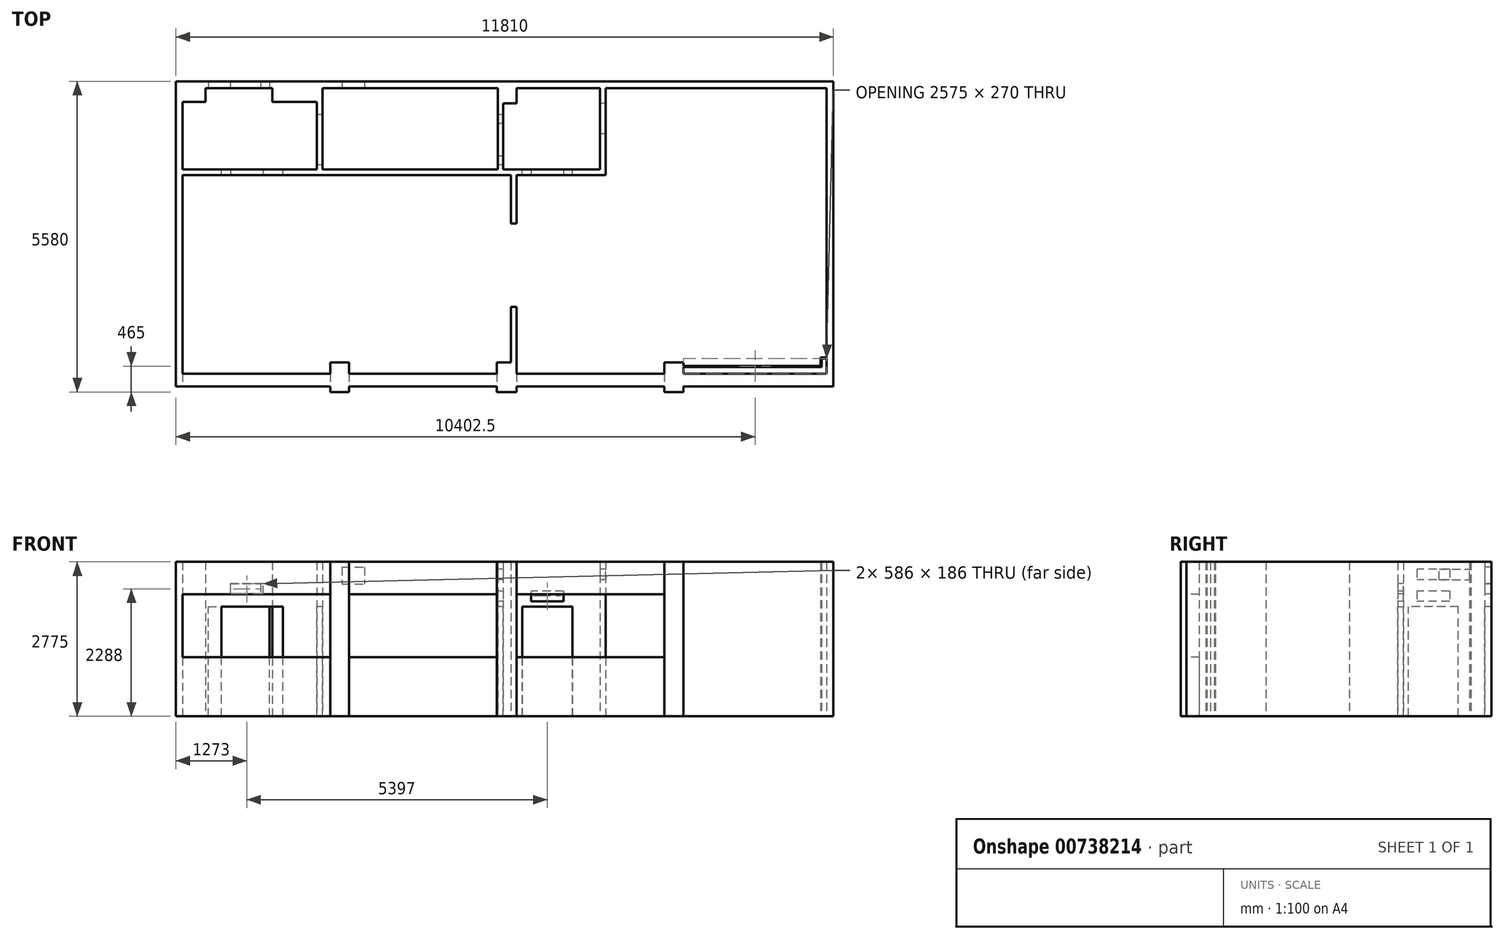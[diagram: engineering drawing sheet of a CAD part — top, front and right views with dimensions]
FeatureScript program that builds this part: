
annotation { "Feature Type Name" : "Feature", "Feature Type Description" : "" }
export const myFeature = defineFeature(function(context is Context, id is Id, definition is map)
    precondition{}
    {
        {
            var Q0;
            Q0=qCreatedBy(makeId("Top.planeOp"),FACE);
            var sketch = newSketch(context, id + "F0", { "sketchPlane" : qUnion([Q0])});
            skLineSegment(sketch, "E0.bottom", {"start": v(0, 0) * mm, "end": v(-5570, 0) * mm});
            skLineSegment(sketch, "E0.top", {"start": v(0, -5240) * mm, "end": v(-2575, -5240) * mm, "construction": true});
            skLineSegment(sketch, "E0.left", {"start": v(0, 0) * mm, "end": v(0, -5240) * mm});
            skLineSegment(sketch, "E0.right", {"start": v(-11570, -250) * mm, "end": v(-11570, -5130) * mm});
            skLineSegment(sketch, "E1.bottom", {"start": v(-11690, 120) * mm, "end": v(120, 120) * mm});
            skLineSegment(sketch, "E1.top", {"start": v(-11690, -5360) * mm, "end": v(-8920, -5360) * mm});
            skLineSegment(sketch, "E1.left", {"start": v(-11690, 120) * mm, "end": v(-11690, -5360) * mm});
            skLineSegment(sketch, "E1.right", {"start": v(120, 120) * mm, "end": v(120, -5360) * mm});
            skLineSegment(sketch, "E2.trimOffspring", {"start": v(-5925, -5240) * mm, "end": v(-8580, -5240) * mm, "construction": true});
            skLineSegment(sketch, "E3.trimOffspring", {"start": v(-5910, 0) * mm, "end": v(-9070, 0) * mm});
            skLineSegment(sketch, "E4", {"start": v(-5910, 0) * mm, "end": v(-5910, -275) * mm});
            skLineSegment(sketch, "E5", {"start": v(-5910, -275) * mm, "end": v(-5570, -275) * mm});
            skLineSegment(sketch, "E6", {"start": v(-5570, -275) * mm, "end": v(-5570, 0) * mm});
            skLineSegment(sketch, "E7", {"start": v(-5925, -5130) * mm, "end": v(-5925, -4930) * mm});
            skLineSegment(sketch, "E8", {"start": v(-5925, -4930) * mm, "end": v(-5570, -4930) * mm});
            skLineSegment(sketch, "E9", {"start": v(-5570, -4930) * mm, "end": v(-5570, -5130) * mm});
            skLineSegment(sketch, "E10.top", {"start": v(-8580, -4930) * mm, "end": v(-8920, -4930) * mm});
            skLineSegment(sketch, "E10.left", {"start": v(-8580, -5130) * mm, "end": v(-8580, -4930) * mm});
            skLineSegment(sketch, "E10.right", {"start": v(-8920, -5130) * mm, "end": v(-8920, -4930) * mm});
            skLineSegment(sketch, "E11.trimOffspring", {"start": v(-8920, -5240) * mm, "end": v(-11570, -5240) * mm, "construction": true});
            skLineSegment(sketch, "E12.top", {"start": v(-11570, -250) * mm, "end": v(-11160, -250) * mm});
            skLineSegment(sketch, "E12.right", {"start": v(-11160, 0) * mm, "end": v(-11160, -250) * mm});
            skLineSegment(sketch, "E13.top", {"start": v(-9960, -250) * mm, "end": v(-9070, -250) * mm});
            skLineSegment(sketch, "E13.left", {"start": v(-9960, 0) * mm, "end": v(-9960, -250) * mm});
            skLineSegment(sketch, "E13.right", {"start": v(-9070, 0) * mm, "end": v(-9070, -250) * mm});
            skLineSegment(sketch, "E14.trimOffspring", {"start": v(-9960, 0) * mm, "end": v(-11160, 0) * mm});
            skLineSegment(sketch, "E15.top", {"start": v(-2915, -4930) * mm, "end": v(-2575, -4930) * mm});
            skLineSegment(sketch, "E15.left", {"start": v(-2915, -5130) * mm, "end": v(-2915, -4930) * mm});
            skLineSegment(sketch, "E15.right", {"start": v(-2575, -5130) * mm, "end": v(-2575, -4930) * mm});
            skLineSegment(sketch, "E16.top", {"start": v(-2575, -5460) * mm, "end": v(-2915, -5460) * mm});
            skLineSegment(sketch, "E16.left", {"start": v(-2575, -5360) * mm, "end": v(-2575, -5460) * mm});
            skLineSegment(sketch, "E16.right", {"start": v(-2915, -5360) * mm, "end": v(-2915, -5460) * mm});
            skLineSegment(sketch, "E17.trimOffspring", {"start": v(-2575, -5360) * mm, "end": v(120, -5360) * mm});
            skLineSegment(sketch, "E18.trimOffspring", {"start": v(-2915, -5240) * mm, "end": v(-5570, -5240) * mm, "construction": true});
            skLineSegment(sketch, "E19.top", {"start": v(-5570, -5460) * mm, "end": v(-5925, -5460) * mm});
            skLineSegment(sketch, "E19.left", {"start": v(-5570, -5360) * mm, "end": v(-5570, -5460) * mm});
            skLineSegment(sketch, "E19.right", {"start": v(-5925, -5360) * mm, "end": v(-5925, -5460) * mm});
            skLineSegment(sketch, "E20.top", {"start": v(-8580, -5460) * mm, "end": v(-8920, -5460) * mm});
            skLineSegment(sketch, "E20.left", {"start": v(-8580, -5360) * mm, "end": v(-8580, -5460) * mm});
            skLineSegment(sketch, "E20.right", {"start": v(-8920, -5360) * mm, "end": v(-8920, -5460) * mm});
            skLineSegment(sketch, "E21.trimOffspring", {"start": v(-8580, -5360) * mm, "end": v(-5925, -5360) * mm});
            skLineSegment(sketch, "E22.trimOffspring", {"start": v(-5570, -5360) * mm, "end": v(-2915, -5360) * mm});
            skLineSegment(sketch, "E23", {"start": v(-11570, -5130) * mm, "end": v(-8920, -5130) * mm});
            skLineSegment(sketch, "E24.trimOffspring", {"start": v(-8580, -5130) * mm, "end": v(-5925, -5130) * mm});
            skLineSegment(sketch, "E25.trimOffspring", {"start": v(-5570, -5130) * mm, "end": v(-2915, -5130) * mm});
            skLineSegment(sketch, "E26.trimOffspring", {"start": v(-2575, -5130) * mm, "end": v(0, -5130) * mm});
            skSolve(sketch);
        }
        {
            var Q0;
            Q0=qSketchRegion(id+"F0",true);
            extrude(context, id + "F1", {"entities" : qUnion([Q0]), "depth" : 2775 * mm, "offsetDistance" : 25 * mm});
        }
        {
            var Q0;
            Q0=makeQuery(id+"F1.opExtrude","SWEPT_FACE",FACE,{"disambiguationData":[OSD([sQuery(id+"F0.wireOp",EDGE,"E0.bottom")])]});
            var sketch = newSketch(context, id + "F2", { "sketchPlane" : qUnion([Q0])});
            skLineSegment(sketch, "E27.bottom", {"start": v(-11110, 0) * mm, "end": v(-10010, 0) * mm});
            skLineSegment(sketch, "E27.top", {"start": v(-11110, 1970) * mm, "end": v(-10010, 1970) * mm});
            skLineSegment(sketch, "E27.left", {"start": v(-11110, 0) * mm, "end": v(-11110, 1970) * mm});
            skLineSegment(sketch, "E27.right", {"start": v(-10010, 0) * mm, "end": v(-10010, 1970) * mm});
            skSolve(sketch);
        }
        {
            var Q0;
            Q0=qSketchRegion(id+"F2",true);
            extrude(context, id + "F3", {"entities" : qUnion([Q0]), "operationType" : NewBodyOperationType.REMOVE, "endBound" : BoundingType.UP_TO_NEXT, "oppositeDirection" : true, "depth" : 25 * mm, "offsetDistance" : 25 * mm});
        }
        {
            var Q0;
            Q0=qCreatedBy(makeId("Top.planeOp"),FACE);
            var sketch = newSketch(context, id + "F4", { "sketchPlane" : qUnion([Q0])});
            skLineSegment(sketch, "E28.top", {"start": v(-5670, -4930) * mm, "end": v(-5570, -4930) * mm});
            skLineSegment(sketch, "E28.left", {"start": v(-5670, -1460) * mm, "end": v(-5670, -4930) * mm});
            skLineSegment(sketch, "E28.right", {"start": v(-5570, -1460) * mm, "end": v(-5570, -4930) * mm});
            skLineSegment(sketch, "E29", {"start": v(-5570, -1460) * mm, "end": v(-5670, -1460) * mm});
            skLineSegment(sketch, "E30", {"start": v(-5670, -2430) * mm, "end": v(-5570, -2430) * mm});
            skLineSegment(sketch, "E31", {"start": v(-5670, -3930) * mm, "end": v(-5570, -3930) * mm});
            skSolve(sketch);
        }
        {
            var Q0;
            {var subQ0=sQuery(id+"F4.wireOp",EDGE,"E28.top");Q0=makeQuery(id+"F4.imprint","IMPRINT",FACE,{"disambiguationData":[TD([[makeQuery(id+"F4.imprint","IMPRINT",EDGE,{"derivedFrom":subQ0}),1.0]])]});}
            var Q1;
            {var subQ0=sQuery(id+"F4.wireOp",EDGE,"E29");Q1=makeQuery(id+"F4.imprint","IMPRINT",FACE,{"disambiguationData":[TD([[makeQuery(id+"F4.imprint","IMPRINT",EDGE,{"derivedFrom":subQ0}),1.0]])]});}
            var Q2;
            Q2=makeQuery(id+"F1.opExtrude","CAP_FACE",FACE,{"disambiguationData":[OSD([sQuery(id+"F0.wireOp",EDGE,"E0.bottom"),sQuery(id+"F0.wireOp",EDGE,"E0.top"),sQuery(id+"F0.wireOp",EDGE,"E0.left"),sQuery(id+"F0.wireOp",EDGE,"E0.right"),sQuery(id+"F0.wireOp",EDGE,"E1.bottom"),sQuery(id+"F0.wireOp",EDGE,"E1.top"),sQuery(id+"F0.wireOp",EDGE,"E1.left"),sQuery(id+"F0.wireOp",EDGE,"E1.right")])],"isStart":false});
            extrude(context, id + "F5", {"entities" : qUnion([Q0, Q1]), "operationType" : NewBodyOperationType.ADD, "endBound" : BoundingType.UP_TO_SURFACE, "depth" : 25 * mm, "endBoundEntityFace" : qUnion([Q2]), "offsetDistance" : 25 * mm});
        }
        {
            var Q0;
            Q0=qCreatedBy(makeId("Top.planeOp"),FACE);
            var sketch = newSketch(context, id + "F6", { "sketchPlane" : qUnion([Q0])});
            skLineSegment(sketch, "E32.bottom", {"start": v(-5670, -1460) * mm, "end": v(-11570, -1460) * mm});
            skLineSegment(sketch, "E32.top", {"start": v(-5670, -1560) * mm, "end": v(-11570, -1560) * mm});
            skLineSegment(sketch, "E32.left", {"start": v(-5670, -1460) * mm, "end": v(-5670, -1560) * mm});
            skLineSegment(sketch, "E32.right", {"start": v(-11570, -1460) * mm, "end": v(-11570, -1560) * mm});
            skSolve(sketch);
        }
        {
            var Q0;
            Q0=makeQuery(id+"F6.imprint","IMPRINT",FACE,{"disambiguationData":[TD([[makeQuery(id+"F6.imprint","IMPRINT",EDGE,{"derivedFrom":sQuery(id+"F6.wireOp",EDGE,"E32.bottom")}),1.0]])]});
            var Q1;
            {var subQ0=sQuery(id+"F0.wireOp",EDGE,"E1.right");var subQ1=sQuery(id+"F0.wireOp",EDGE,"E1.left");var subQ2=sQuery(id+"F0.wireOp",EDGE,"E1.top");var subQ3=sQuery(id+"F0.wireOp",EDGE,"E1.bottom");var subQ4=sQuery(id+"F0.wireOp",EDGE,"E0.right");var subQ5=sQuery(id+"F0.wireOp",EDGE,"E0.left");var subQ6=sQuery(id+"F0.wireOp",EDGE,"E0.top");var subQ7=sQuery(id+"F0.wireOp",EDGE,"E0.bottom");Q1=makeQuery(id+"F5.boolean.opBoolean","MERGE",FACE,{"derivedFrom":[makeQuery(id+"F1.opExtrude","CAP_FACE",FACE,{"disambiguationData":[OSD([subQ7,subQ6,subQ5,subQ4,subQ3,subQ2,subQ1,subQ0])],"isStart":false}),makeQuery(id+"F5.opExtrude","CAP_FACE",FACE,{"disambiguationData":[OSD([subQ7,subQ6,subQ5,subQ4,subQ3,subQ2,subQ1,subQ0])],"isStart":false})]});}
            extrude(context, id + "F7", {"entities" : qUnion([Q0]), "operationType" : NewBodyOperationType.ADD, "endBound" : BoundingType.UP_TO_SURFACE, "depth" : 25 * mm, "endBoundEntityFace" : qUnion([Q1]), "offsetDistance" : 25 * mm});
        }
        {
            var Q0;
            Q0=qCreatedBy(makeId("Top.planeOp"),FACE);
            var sketch = newSketch(context, id + "F8", { "sketchPlane" : qUnion([Q0])});
            skLineSegment(sketch, "E33.bottom", {"start": v(-9060, 0) * mm, "end": v(-9160, 0) * mm});
            skLineSegment(sketch, "E33.top", {"start": v(-9060, -1460) * mm, "end": v(-9160, -1460) * mm});
            skLineSegment(sketch, "E33.left", {"start": v(-9060, 0) * mm, "end": v(-9060, -1460) * mm});
            skLineSegment(sketch, "E33.right", {"start": v(-9160, 0) * mm, "end": v(-9160, -1460) * mm});
            skSolve(sketch);
        }
        {
            var Q0;
            Q0=makeQuery(id+"F8.imprint","IMPRINT",FACE,{"disambiguationData":[TD([[makeQuery(id+"F8.imprint","IMPRINT",EDGE,{"derivedFrom":sQuery(id+"F8.wireOp",EDGE,"E33.bottom")}),1.0]])]});
            var Q1;
            {var subQ0=sQuery(id+"F0.wireOp",EDGE,"E1.right");var subQ1=sQuery(id+"F0.wireOp",EDGE,"E1.left");var subQ2=sQuery(id+"F0.wireOp",EDGE,"E1.top");var subQ3=sQuery(id+"F0.wireOp",EDGE,"E1.bottom");var subQ4=sQuery(id+"F0.wireOp",EDGE,"E0.right");var subQ5=sQuery(id+"F0.wireOp",EDGE,"E0.left");var subQ6=sQuery(id+"F0.wireOp",EDGE,"E0.top");var subQ7=sQuery(id+"F0.wireOp",EDGE,"E0.bottom");Q1=makeQuery(id+"F7.boolean.opBoolean","MERGE",FACE,{"derivedFrom":[makeQuery(id+"F5.boolean.opBoolean","MERGE",FACE,{"derivedFrom":[makeQuery(id+"F1.opExtrude","CAP_FACE",FACE,{"disambiguationData":[OSD([subQ7,subQ6,subQ5,subQ4,subQ3,subQ2,subQ1,subQ0])],"isStart":false}),makeQuery(id+"F5.opExtrude","CAP_FACE",FACE,{"disambiguationData":[OSD([subQ7,subQ6,subQ5,subQ4,subQ3,subQ2,subQ1,subQ0])],"isStart":false})]}),makeQuery(id+"F7.opExtrude","CAP_FACE",FACE,{"disambiguationData":[OSD([subQ7,subQ6,subQ5,subQ4,subQ3,subQ2,subQ1,subQ0])],"isStart":false})]});}
            extrude(context, id + "F9", {"entities" : qUnion([Q0]), "operationType" : NewBodyOperationType.ADD, "endBound" : BoundingType.UP_TO_SURFACE, "depth" : 25 * mm, "endBoundEntityFace" : qUnion([Q1]), "offsetDistance" : 25 * mm});
        }
        {
            var Q0;
            {var subQ0=sQuery(id+"F0.wireOp",EDGE,"E0.right");var subQ8=sQuery(id+"F6.wireOp",EDGE,"E32.bottom");Q0=makeQuery(id+"F9.boolean.opBoolean","SPLIT",FACE,{"disambiguationData":[TD([makeQuery(id+"F1.opExtrude","SWEPT_FACE",FACE,{"disambiguationData":[OSD([subQ0])]})])],"derivedFrom":makeQuery(id+"F7.opExtrude","SWEPT_FACE",FACE,{"disambiguationData":[OSD([subQ8])]})});}
            var sketch = newSketch(context, id + "F10", { "sketchPlane" : qUnion([Q0])});
            skLineSegment(sketch, "E34.bottom", {"start": v(9770, 0) * mm, "end": v(10870, 0) * mm});
            skLineSegment(sketch, "E34.top", {"start": v(9770, 1970) * mm, "end": v(10870, 1970) * mm});
            skLineSegment(sketch, "E34.left", {"start": v(9770, 0) * mm, "end": v(9770, 1970) * mm});
            skLineSegment(sketch, "E34.right", {"start": v(10870, 0) * mm, "end": v(10870, 1970) * mm});
            skSolve(sketch);
        }
        {
            var Q0;
            Q0=makeQuery(id+"F10.imprint","IMPRINT",FACE,{"disambiguationData":[TD([[makeQuery(id+"F10.imprint","IMPRINT",EDGE,{"derivedFrom":sQuery(id+"F10.wireOp",EDGE,"E34.bottom")}),1.0]])]});
            extrude(context, id + "F11", {"entities" : qUnion([Q0]), "operationType" : NewBodyOperationType.REMOVE, "endBound" : BoundingType.UP_TO_NEXT, "oppositeDirection" : true, "depth" : 25 * mm, "offsetDistance" : 25 * mm});
        }
        {
            var Q0;
            Q0=makeQuery(id+"F9.opExtrude","SWEPT_FACE",FACE,{"disambiguationData":[OSD([sQuery(id+"F8.wireOp",EDGE,"E33.right")])]});
            var sketch = newSketch(context, id + "F12", { "sketchPlane" : qUnion([Q0])});
            skLineSegment(sketch, "E35.bottom", {"start": v(475, 0) * mm, "end": v(1375, 0) * mm});
            skLineSegment(sketch, "E35.top", {"start": v(475, 1970) * mm, "end": v(1375, 1970) * mm});
            skLineSegment(sketch, "E35.left", {"start": v(475, 0) * mm, "end": v(475, 1970) * mm});
            skLineSegment(sketch, "E35.right", {"start": v(1375, 0) * mm, "end": v(1375, 1970) * mm});
            skPoint(sketch, "E36.startSnap0", {"position": v(925, 1970) * mm});
            skSolve(sketch);
        }
        {
            var Q0;
            Q0=qSketchRegion(id+"F12",true);
            extrude(context, id + "F13", {"entities" : qUnion([Q0]), "operationType" : NewBodyOperationType.REMOVE, "endBound" : BoundingType.UP_TO_NEXT, "oppositeDirection" : true, "depth" : 25 * mm, "offsetDistance" : 25 * mm});
        }
        {
            var Q0;
            Q0=qCreatedBy(makeId("Top.planeOp"),FACE);
            var sketch = newSketch(context, id + "F14", { "sketchPlane" : qUnion([Q0])});
            skLineSegment(sketch, "E37.bottom", {"start": v(-5910, -275) * mm, "end": v(-5810, -275) * mm});
            skLineSegment(sketch, "E37.top", {"start": v(-5910, -1460) * mm, "end": v(-5810, -1460) * mm});
            skLineSegment(sketch, "E37.left", {"start": v(-5910, -275) * mm, "end": v(-5910, -1460) * mm});
            skLineSegment(sketch, "E37.right", {"start": v(-5810, -275) * mm, "end": v(-5810, -1460) * mm});
            skSolve(sketch);
        }
        {
            var Q0;
            Q0=qSketchRegion(id+"F14",true);
            var Q1;
            {var subQ0=sQuery(id+"F0.wireOp",EDGE,"E3.trimOffspring");var subQ1=sQuery(id+"F0.wireOp",EDGE,"E2.trimOffspring");var subQ2=sQuery(id+"F0.wireOp",EDGE,"dA5mFhwm-C5pU-s43x-tqTS-3jepumlIrKXL.right");var subQ3=sQuery(id+"F0.wireOp",EDGE,"dA5mFhwm-C5pU-s43x-tqTS-3jepumlIrKXL.left");var subQ4=sQuery(id+"F0.wireOp",EDGE,"dA5mFhwm-C5pU-s43x-tqTS-3jepumlIrKXL.top");var subQ5=sQuery(id+"F0.wireOp",EDGE,"zGKuHS85-YCsc-AVKT-CzAw-lwCyFNVVRMQ6.right");var subQ6=sQuery(id+"F0.wireOp",EDGE,"zGKuHS85-YCsc-AVKT-CzAw-lwCyFNVVRMQ6.left");var subQ7=sQuery(id+"F0.wireOp",EDGE,"zGKuHS85-YCsc-AVKT-CzAw-lwCyFNVVRMQ6.top");var subQ8=sQuery(id+"F0.wireOp",EDGE,"E1.right");var subQ9=sQuery(id+"F0.wireOp",EDGE,"E1.left");var subQ10=sQuery(id+"F0.wireOp",EDGE,"E1.top");var subQ11=sQuery(id+"F0.wireOp",EDGE,"E1.bottom");var subQ12=sQuery(id+"F0.wireOp",EDGE,"E0.right");var subQ13=sQuery(id+"F0.wireOp",EDGE,"E0.left");var subQ14=sQuery(id+"F0.wireOp",EDGE,"E0.top");var subQ15=sQuery(id+"F0.wireOp",EDGE,"E0.bottom");Q1=makeQuery(id+"F9.boolean.opBoolean","MERGE",FACE,{"derivedFrom":[makeQuery(id+"F7.boolean.opBoolean","MERGE",FACE,{"derivedFrom":[makeQuery(id+"F5.boolean.opBoolean","MERGE",FACE,{"derivedFrom":[makeQuery(id+"F1.opExtrude","CAP_FACE",FACE,{"disambiguationData":[OSD([subQ15,subQ14,subQ13,subQ12,subQ11,subQ10,subQ9,subQ8,subQ7,subQ6,subQ5,subQ4,subQ3,subQ2,subQ1,subQ0])],"isStart":false}),makeQuery(id+"F5.opExtrude","CAP_FACE",FACE,{"disambiguationData":[OSD([subQ15,subQ14,subQ13,subQ12,subQ11,subQ10,subQ9,subQ8,subQ7,subQ6,subQ5,subQ4,subQ3,subQ2,subQ1,subQ0])],"isStart":false})]}),makeQuery(id+"F7.opExtrude","CAP_FACE",FACE,{"disambiguationData":[OSD([subQ15,subQ14,subQ13,subQ12,subQ11,subQ10,subQ9,subQ8,subQ7,subQ6,subQ5,subQ4,subQ3,subQ2,subQ1,subQ0])],"isStart":false})]}),makeQuery(id+"F9.opExtrude","CAP_FACE",FACE,{"disambiguationData":[OSD([subQ15,subQ14,subQ13,subQ12,subQ11,subQ10,subQ9,subQ8,subQ7,subQ6,subQ5,subQ4,subQ3,subQ2,subQ1,subQ0])],"isStart":false})]});}
            extrude(context, id + "F15", {"entities" : qUnion([Q0]), "operationType" : NewBodyOperationType.ADD, "endBound" : BoundingType.UP_TO_SURFACE, "depth" : 25 * mm, "endBoundEntityFace" : qUnion([Q1]), "offsetDistance" : 25 * mm});
        }
        {
            var Q0;
            Q0=makeQuery(id+"F15.boolean.opBoolean","MERGE",FACE,{"derivedFrom":[makeQuery(id+"F1.opExtrude","SWEPT_FACE",FACE,{"disambiguationData":[OSD([sQuery(id+"F0.wireOp",EDGE,"zGKuHS85-YCsc-AVKT-CzAw-lwCyFNVVRMQ6.right")])]}),makeQuery(id+"F15.opExtrude","SWEPT_FACE",FACE,{"disambiguationData":[OSD([sQuery(id+"F14.wireOp",EDGE,"E37.left")])]})]});
            var sketch = newSketch(context, id + "F16", { "sketchPlane" : qUnion([Q0])});
            skLineSegment(sketch, "E38.bottom", {"start": v(475, 0) * mm, "end": v(1375, 0) * mm});
            skLineSegment(sketch, "E38.top", {"start": v(475, 1970) * mm, "end": v(1375, 1970) * mm});
            skLineSegment(sketch, "E38.left", {"start": v(475, 0) * mm, "end": v(475, 1970) * mm});
            skLineSegment(sketch, "E38.right", {"start": v(1375, 0) * mm, "end": v(1375, 1970) * mm});
            skSolve(sketch);
        }
        {
            var Q0;
            Q0=qSketchRegion(id+"F16",true);
            var Q1;
            Q1=makeQuery(id+"F15.opExtrude","SWEPT_FACE",FACE,{"disambiguationData":[OSD([sQuery(id+"F14.wireOp",EDGE,"E37.right")])]});
            extrude(context, id + "F17", {"entities" : qUnion([Q0]), "operationType" : NewBodyOperationType.REMOVE, "endBound" : BoundingType.UP_TO_SURFACE, "oppositeDirection" : true, "depth" : 25 * mm, "endBoundEntityFace" : qUnion([Q1]), "offsetDistance" : 25 * mm});
        }
        {
            var Q0;
            Q0=qCreatedBy(makeId("Top.planeOp"),FACE);
            var sketch = newSketch(context, id + "F18", { "sketchPlane" : qUnion([Q0])});
            skLineSegment(sketch, "E39", {"start": v(-5570, -1560) * mm, "end": v(-3970, -1560) * mm});
            skLineSegment(sketch, "E40", {"start": v(-3970, -1560) * mm, "end": v(-3970, 0) * mm});
            skLineSegment(sketch, "E41", {"start": v(-3970, 0) * mm, "end": v(-4070, 0) * mm});
            skLineSegment(sketch, "E42", {"start": v(-4070, 0) * mm, "end": v(-4070, -1460) * mm});
            skLineSegment(sketch, "E43", {"start": v(-4070, -1460) * mm, "end": v(-5570, -1460) * mm});
            skLineSegment(sketch, "E44", {"start": v(-5570, -1460) * mm, "end": v(-5570, -1560) * mm});
            skSolve(sketch);
        }
        {
            var Q0;
            Q0=makeQuery(id+"F18.imprint","IMPRINT",FACE,{"disambiguationData":[TD([[makeQuery(id+"F18.imprint","IMPRINT",EDGE,{"derivedFrom":sQuery(id+"F18.wireOp",EDGE,"E39")}),1.0]])]});
            var Q1;
            {var subQ0=sQuery(id+"F0.wireOp",EDGE,"E3.trimOffspring");var subQ1=sQuery(id+"F0.wireOp",EDGE,"E2.trimOffspring");var subQ2=sQuery(id+"F0.wireOp",EDGE,"dA5mFhwm-C5pU-s43x-tqTS-3jepumlIrKXL.right");var subQ3=sQuery(id+"F0.wireOp",EDGE,"dA5mFhwm-C5pU-s43x-tqTS-3jepumlIrKXL.left");var subQ4=sQuery(id+"F0.wireOp",EDGE,"dA5mFhwm-C5pU-s43x-tqTS-3jepumlIrKXL.top");var subQ5=sQuery(id+"F0.wireOp",EDGE,"zGKuHS85-YCsc-AVKT-CzAw-lwCyFNVVRMQ6.right");var subQ6=sQuery(id+"F0.wireOp",EDGE,"zGKuHS85-YCsc-AVKT-CzAw-lwCyFNVVRMQ6.left");var subQ7=sQuery(id+"F0.wireOp",EDGE,"zGKuHS85-YCsc-AVKT-CzAw-lwCyFNVVRMQ6.top");var subQ8=sQuery(id+"F0.wireOp",EDGE,"E1.right");var subQ9=sQuery(id+"F0.wireOp",EDGE,"E1.left");var subQ10=sQuery(id+"F0.wireOp",EDGE,"E1.top");var subQ11=sQuery(id+"F0.wireOp",EDGE,"E1.bottom");var subQ12=sQuery(id+"F0.wireOp",EDGE,"E0.right");var subQ13=sQuery(id+"F0.wireOp",EDGE,"E0.left");var subQ14=sQuery(id+"F0.wireOp",EDGE,"E0.top");var subQ15=sQuery(id+"F0.wireOp",EDGE,"E0.bottom");Q1=makeQuery(id+"F15.boolean.opBoolean","MERGE",FACE,{"derivedFrom":[makeQuery(id+"F9.boolean.opBoolean","MERGE",FACE,{"derivedFrom":[makeQuery(id+"F7.boolean.opBoolean","MERGE",FACE,{"derivedFrom":[makeQuery(id+"F5.boolean.opBoolean","MERGE",FACE,{"derivedFrom":[makeQuery(id+"F1.opExtrude","CAP_FACE",FACE,{"disambiguationData":[OSD([subQ15,subQ14,subQ13,subQ12,subQ11,subQ10,subQ9,subQ8,subQ7,subQ6,subQ5,subQ4,subQ3,subQ2,subQ1,subQ0])],"isStart":false}),makeQuery(id+"F5.opExtrude","CAP_FACE",FACE,{"disambiguationData":[OSD([subQ15,subQ14,subQ13,subQ12,subQ11,subQ10,subQ9,subQ8,subQ7,subQ6,subQ5,subQ4,subQ3,subQ2,subQ1,subQ0])],"isStart":false})]}),makeQuery(id+"F7.opExtrude","CAP_FACE",FACE,{"disambiguationData":[OSD([subQ15,subQ14,subQ13,subQ12,subQ11,subQ10,subQ9,subQ8,subQ7,subQ6,subQ5,subQ4,subQ3,subQ2,subQ1,subQ0])],"isStart":false})]}),makeQuery(id+"F9.opExtrude","CAP_FACE",FACE,{"disambiguationData":[OSD([subQ15,subQ14,subQ13,subQ12,subQ11,subQ10,subQ9,subQ8,subQ7,subQ6,subQ5,subQ4,subQ3,subQ2,subQ1,subQ0])],"isStart":false})]}),makeQuery(id+"F15.opExtrude","CAP_FACE",FACE,{"disambiguationData":[OSD([subQ15,subQ14,subQ13,subQ12,subQ11,subQ10,subQ9,subQ8,subQ7,subQ6,subQ5,subQ4,subQ3,subQ2,subQ1,subQ0])],"isStart":false})]});}
            extrude(context, id + "F19", {"entities" : qUnion([Q0]), "operationType" : NewBodyOperationType.ADD, "endBound" : BoundingType.UP_TO_SURFACE, "depth" : 25 * mm, "endBoundEntityFace" : qUnion([Q1]), "offsetDistance" : 25 * mm});
        }
        {
            var Q0;
            Q0=makeQuery(id+"F19.opExtrude","SWEPT_FACE",FACE,{"disambiguationData":[OSD([sQuery(id+"F18.wireOp",EDGE,"E43")])]});
            var sketch = newSketch(context, id + "F20", { "sketchPlane" : qUnion([Q0])});
            skLineSegment(sketch, "E45.bottom", {"start": v(4570, 0) * mm, "end": v(5470, 0) * mm});
            skLineSegment(sketch, "E45.top", {"start": v(4570, 1970) * mm, "end": v(5470, 1970) * mm});
            skLineSegment(sketch, "E45.left", {"start": v(4570, 0) * mm, "end": v(4570, 1970) * mm});
            skLineSegment(sketch, "E45.right", {"start": v(5470, 0) * mm, "end": v(5470, 1970) * mm});
            skSolve(sketch);
        }
        {
            var Q0;
            Q0=makeQuery(id+"F20.imprint","IMPRINT",FACE,{"disambiguationData":[TD([[makeQuery(id+"F20.imprint","IMPRINT",EDGE,{"derivedFrom":sQuery(id+"F20.wireOp",EDGE,"E45.bottom")}),1.0]])]});
            extrude(context, id + "F21", {"entities" : qUnion([Q0]), "operationType" : NewBodyOperationType.REMOVE, "endBound" : BoundingType.UP_TO_NEXT, "oppositeDirection" : true, "depth" : 25 * mm, "offsetDistance" : 25 * mm});
        }
        {
            var Q0;
            Q0=makeQuery(id+"F1.opExtrude","SWEPT_FACE",FACE,{"disambiguationData":[OSD([sQuery(id+"F0.wireOp",EDGE,"E1.top")])]});
            var sketch = newSketch(context, id + "F22", { "sketchPlane" : qUnion([Q0])});
            skLineSegment(sketch, "E46.bottom", {"start": v(-2915, 2190) * mm, "end": v(-5570, 2190) * mm});
            skLineSegment(sketch, "E46.top", {"start": v(-2915, 1060) * mm, "end": v(-5570, 1060) * mm});
            skLineSegment(sketch, "E46.left", {"start": v(-2915, 2190) * mm, "end": v(-2915, 1060) * mm});
            skLineSegment(sketch, "E46.right", {"start": v(-5570, 2190) * mm, "end": v(-5570, 1060) * mm});
            skSolve(sketch);
        }
        {
            var Q0;
            Q0=makeQuery(id+"F22.imprint","IMPRINT",FACE,{"disambiguationData":[TD([[makeQuery(id+"F22.imprint","IMPRINT",EDGE,{"derivedFrom":sQuery(id+"F22.wireOp",EDGE,"UQFrSV9A-AeNk-hTGs-XUq7-kkI5QUDZIYbv.bottom")}),1.0]])]});
            var Q1;
            Q1=makeQuery(id+"F22.imprint","IMPRINT",FACE,{"disambiguationData":[TD([[makeQuery(id+"F22.imprint","IMPRINT",EDGE,{"derivedFrom":sQuery(id+"F22.wireOp",EDGE,"E46.bottom")}),1.0]])]});
            extrude(context, id + "F23", {"entities" : qUnion([Q0, Q1]), "operationType" : NewBodyOperationType.REMOVE, "endBound" : BoundingType.UP_TO_NEXT, "oppositeDirection" : true, "depth" : 25 * mm, "offsetDistance" : 25 * mm});
        }
        {
            var Q0;
            Q0=makeQuery(id+"F1.opExtrude","SWEPT_FACE",FACE,{"disambiguationData":[OSD([sQuery(id+"F0.wireOp",EDGE,"E1.top")])]});
            var sketch = newSketch(context, id + "F24", { "sketchPlane" : qUnion([Q0])});
            skLineSegment(sketch, "E47.bottom", {"start": v(-5925, 2190) * mm, "end": v(-8580, 2190) * mm});
            skLineSegment(sketch, "E47.top", {"start": v(-5925, 1060) * mm, "end": v(-8580, 1060) * mm});
            skLineSegment(sketch, "E47.left", {"start": v(-5925, 2190) * mm, "end": v(-5925, 1060) * mm});
            skLineSegment(sketch, "E47.right", {"start": v(-8580, 2190) * mm, "end": v(-8580, 1060) * mm});
            skLineSegment(sketch, "E48.bottom", {"start": v(-8920, 2190) * mm, "end": v(-11570, 2190) * mm});
            skLineSegment(sketch, "E48.top", {"start": v(-8920, 1060) * mm, "end": v(-11570, 1060) * mm});
            skLineSegment(sketch, "E48.left", {"start": v(-8920, 2190) * mm, "end": v(-8920, 1060) * mm});
            skLineSegment(sketch, "E48.right", {"start": v(-11570, 2190) * mm, "end": v(-11570, 1060) * mm});
            skSolve(sketch);
        }
        {
            var Q0;
            Q0=makeQuery(id+"F24.imprint","IMPRINT",FACE,{"disambiguationData":[TD([[makeQuery(id+"F24.imprint","IMPRINT",EDGE,{"derivedFrom":sQuery(id+"F24.wireOp",EDGE,"E48.bottom")}),1.0]])]});
            var Q1;
            Q1=makeQuery(id+"F24.imprint","IMPRINT",FACE,{"disambiguationData":[TD([[makeQuery(id+"F24.imprint","IMPRINT",EDGE,{"derivedFrom":sQuery(id+"F24.wireOp",EDGE,"E47.bottom")}),1.0]])]});
            extrude(context, id + "F25", {"entities" : qUnion([Q0, Q1]), "operationType" : NewBodyOperationType.REMOVE, "endBound" : BoundingType.UP_TO_NEXT, "oppositeDirection" : true, "depth" : 25 * mm, "offsetDistance" : 25 * mm});
        }
        {
            var Q0;
            Q0=makeQuery(id+"F1.opExtrude","SWEPT_FACE",FACE,{"disambiguationData":[OSD([sQuery(id+"F0.wireOp",EDGE,"E3.trimOffspring")])]});
            var sketch = newSketch(context, id + "F26", { "sketchPlane" : qUnion([Q0])});
            skLineSegment(sketch, "E49.bottom", {"start": v(-8710, 2680) * mm, "end": v(-8304, 2680) * mm});
            skLineSegment(sketch, "E49.top", {"start": v(-8710, 2374) * mm, "end": v(-8304, 2374) * mm});
            skLineSegment(sketch, "E49.left", {"start": v(-8710, 2680) * mm, "end": v(-8710, 2374) * mm});
            skLineSegment(sketch, "E49.right", {"start": v(-8304, 2680) * mm, "end": v(-8304, 2374) * mm});
            skSolve(sketch);
        }
        {
            var Q0;
            Q0=makeQuery(id+"F26.imprint","IMPRINT",FACE,{"disambiguationData":[TD([[makeQuery(id+"F26.imprint","IMPRINT",EDGE,{"derivedFrom":sQuery(id+"F26.wireOp",EDGE,"E49.bottom")}),-1.0]])]});
            extrude(context, id + "F27", {"entities" : qUnion([Q0]), "operationType" : NewBodyOperationType.REMOVE, "endBound" : BoundingType.UP_TO_NEXT, "oppositeDirection" : true, "depth" : 25 * mm, "offsetDistance" : 25 * mm});
        }
        {
            var Q0;
            Q0=makeQuery(id+"F19.opExtrude","SWEPT_FACE",FACE,{"disambiguationData":[OSD([sQuery(id+"F18.wireOp",EDGE,"E42")])]});
            var sketch = newSketch(context, id + "F28", { "sketchPlane" : qUnion([Q0])});
            skLineSegment(sketch, "E50.bottom", {"start": v(275, 2640) * mm, "end": v(821, 2640) * mm});
            skLineSegment(sketch, "E50.top", {"start": v(275, 2454) * mm, "end": v(821, 2454) * mm});
            skLineSegment(sketch, "E50.left", {"start": v(275, 2640) * mm, "end": v(275, 2454) * mm});
            skLineSegment(sketch, "E50.right", {"start": v(821, 2640) * mm, "end": v(821, 2454) * mm});
            skSolve(sketch);
        }
        {
            var Q0;
            Q0=makeQuery(id+"F28.imprint","IMPRINT",FACE,{"disambiguationData":[TD([[makeQuery(id+"F28.imprint","IMPRINT",EDGE,{"derivedFrom":sQuery(id+"F28.wireOp",EDGE,"E50.bottom")}),-1.0]])]});
            extrude(context, id + "F29", {"entities" : qUnion([Q0]), "operationType" : NewBodyOperationType.REMOVE, "endBound" : BoundingType.UP_TO_NEXT, "oppositeDirection" : true, "depth" : 25 * mm, "offsetDistance" : 25 * mm});
        }
        {
            var Q0;
            Q0=makeQuery(id+"F15.boolean.opBoolean","MERGE",FACE,{"derivedFrom":[makeQuery(id+"F1.opExtrude","SWEPT_FACE",FACE,{"disambiguationData":[OSD([sQuery(id+"F0.wireOp",EDGE,"E4")])]}),makeQuery(id+"F15.opExtrude","SWEPT_FACE",FACE,{"disambiguationData":[OSD([sQuery(id+"F14.wireOp",EDGE,"E37.left")])]})]});
            var sketch = newSketch(context, id + "F30", { "sketchPlane" : qUnion([Q0])});
            skLineSegment(sketch, "E51.bottom", {"start": v(632, 2640) * mm, "end": v(1218, 2640) * mm});
            skLineSegment(sketch, "E51.top", {"start": v(632, 2454) * mm, "end": v(1218, 2454) * mm});
            skLineSegment(sketch, "E51.left", {"start": v(632, 2640) * mm, "end": v(632, 2454) * mm});
            skLineSegment(sketch, "E51.right", {"start": v(1218, 2640) * mm, "end": v(1218, 2454) * mm});
            skLineSegment(sketch, "E52.bottom", {"start": v(632, 2251) * mm, "end": v(1218, 2251) * mm});
            skLineSegment(sketch, "E52.top", {"start": v(632, 2065) * mm, "end": v(1218, 2065) * mm});
            skLineSegment(sketch, "E52.left", {"start": v(632, 2251) * mm, "end": v(632, 2065) * mm});
            skLineSegment(sketch, "E52.right", {"start": v(1218, 2251) * mm, "end": v(1218, 2065) * mm});
            skSolve(sketch);
        }
        {
            var Q0;
            Q0=makeQuery(id+"F30.imprint","IMPRINT",FACE,{"disambiguationData":[TD([[makeQuery(id+"F30.imprint","IMPRINT",EDGE,{"derivedFrom":sQuery(id+"F30.wireOp",EDGE,"E51.bottom")}),-1.0]])]});
            var Q1;
            Q1=makeQuery(id+"F30.imprint","IMPRINT",FACE,{"disambiguationData":[TD([[makeQuery(id+"F30.imprint","IMPRINT",EDGE,{"derivedFrom":sQuery(id+"F30.wireOp",EDGE,"E52.bottom")}),-1.0]])]});
            extrude(context, id + "F31", {"entities" : qUnion([Q0, Q1]), "operationType" : NewBodyOperationType.REMOVE, "endBound" : BoundingType.UP_TO_NEXT, "oppositeDirection" : true, "depth" : 25 * mm, "offsetDistance" : 25 * mm});
        }
        {
            var Q0;
            Q0=makeQuery(id+"F1.opExtrude","SWEPT_FACE",FACE,{"disambiguationData":[OSD([sQuery(id+"F0.wireOp",EDGE,"E14.trimOffspring")])]});
            var sketch = newSketch(context, id + "F32", { "sketchPlane" : qUnion([Q0])});
            skLineSegment(sketch, "E53.bottom", {"start": v(-10716, 2381) * mm, "end": v(-10170, 2381) * mm});
            skLineSegment(sketch, "E53.top", {"start": v(-10716, 2195) * mm, "end": v(-10170, 2195) * mm});
            skLineSegment(sketch, "E53.left", {"start": v(-10716, 2381) * mm, "end": v(-10716, 2195) * mm});
            skLineSegment(sketch, "E53.right", {"start": v(-10170, 2381) * mm, "end": v(-10170, 2195) * mm});
            skSolve(sketch);
        }
        {
            var Q0;
            Q0=makeQuery(id+"F32.imprint","IMPRINT",FACE,{"disambiguationData":[TD([[makeQuery(id+"F32.imprint","IMPRINT",EDGE,{"derivedFrom":sQuery(id+"F32.wireOp",EDGE,"E53.bottom")}),-1.0]])]});
            extrude(context, id + "F33", {"entities" : qUnion([Q0]), "operationType" : NewBodyOperationType.REMOVE, "endBound" : BoundingType.UP_TO_NEXT, "oppositeDirection" : true, "depth" : 25 * mm, "offsetDistance" : 25 * mm});
        }
        {
            var Q0;
            Q0=makeQuery(id+"F7.opExtrude","SWEPT_FACE",FACE,{"disambiguationData":[OSD([sQuery(id+"F6.wireOp",EDGE,"E32.top")])]});
            var sketch = newSketch(context, id + "F34", { "sketchPlane" : qUnion([Q0])});
            skLineSegment(sketch, "E54.bottom", {"start": v(-10710, 2381) * mm, "end": v(-10124, 2381) * mm});
            skLineSegment(sketch, "E54.top", {"start": v(-10710, 2195) * mm, "end": v(-10124, 2195) * mm});
            skLineSegment(sketch, "E54.left", {"start": v(-10710, 2381) * mm, "end": v(-10710, 2195) * mm});
            skLineSegment(sketch, "E54.right", {"start": v(-10124, 2381) * mm, "end": v(-10124, 2195) * mm});
            skSolve(sketch);
        }
        {
            var Q0;
            Q0=makeQuery(id+"F34.imprint","IMPRINT",FACE,{"disambiguationData":[TD([[makeQuery(id+"F34.imprint","IMPRINT",EDGE,{"derivedFrom":sQuery(id+"F34.wireOp",EDGE,"E54.bottom")}),-1.0]])]});
            extrude(context, id + "F35", {"entities" : qUnion([Q0]), "operationType" : NewBodyOperationType.REMOVE, "endBound" : BoundingType.UP_TO_NEXT, "oppositeDirection" : true, "depth" : 25 * mm, "offsetDistance" : 25 * mm});
        }
        {
            var Q0;
            Q0=qCreatedBy(makeId("Top.planeOp"),FACE);
            var sketch = newSketch(context, id + "F36", { "sketchPlane" : qUnion([Q0])});
            skLineSegment(sketch, "E55.bottom", {"start": v(-2575, -4990) * mm, "end": v(-110, -4990) * mm});
            skLineSegment(sketch, "E55.top", {"start": v(-2575, -5010) * mm, "end": v(-90, -5010) * mm});
            skLineSegment(sketch, "E55.left", {"start": v(-2575, -4990) * mm, "end": v(-2575, -5010) * mm});
            skLineSegment(sketch, "E56.bottom", {"start": v(0, -4840) * mm, "end": v(-110, -4840) * mm});
            skLineSegment(sketch, "E56.left", {"start": v(0, -4840) * mm, "end": v(0, -4860) * mm});
            skLineSegment(sketch, "E56.right", {"start": v(-110, -4840) * mm, "end": v(-110, -4990) * mm});
            skLineSegment(sketch, "E57.0", {"start": v(-90, -4860) * mm, "end": v(-90, -5010) * mm});
            skLineSegment(sketch, "E57.1", {"start": v(0, -4860) * mm, "end": v(-90, -4860) * mm});
            skSolve(sketch);
        }
        {
            var Q0;
            Q0=makeQuery(id+"F36.imprint","IMPRINT",FACE,{"disambiguationData":[TD([[makeQuery(id+"F36.imprint","IMPRINT",EDGE,{"derivedFrom":sQuery(id+"F36.wireOp",EDGE,"E55.bottom")}),-1.0]])]});
            var Q1;
            {var subQ0=sQuery(id+"F0.wireOp",EDGE,"E26.trimOffspring");var subQ1=sQuery(id+"F0.wireOp",EDGE,"E25.trimOffspring");var subQ2=sQuery(id+"F0.wireOp",EDGE,"E24.trimOffspring");var subQ3=sQuery(id+"F0.wireOp",EDGE,"E23");var subQ4=sQuery(id+"F0.wireOp",EDGE,"E22.trimOffspring");var subQ5=sQuery(id+"F0.wireOp",EDGE,"E21.trimOffspring");var subQ6=sQuery(id+"F0.wireOp",EDGE,"E20.right");var subQ7=sQuery(id+"F0.wireOp",EDGE,"E20.left");var subQ8=sQuery(id+"F0.wireOp",EDGE,"E20.top");var subQ9=sQuery(id+"F0.wireOp",EDGE,"E19.right");var subQ10=sQuery(id+"F0.wireOp",EDGE,"E19.left");var subQ11=sQuery(id+"F0.wireOp",EDGE,"E19.top");var subQ12=sQuery(id+"F0.wireOp",EDGE,"E17.trimOffspring");var subQ13=sQuery(id+"F0.wireOp",EDGE,"E16.right");var subQ14=sQuery(id+"F0.wireOp",EDGE,"E16.left");var subQ15=sQuery(id+"F0.wireOp",EDGE,"E16.top");var subQ16=sQuery(id+"F0.wireOp",EDGE,"E15.right");var subQ17=sQuery(id+"F0.wireOp",EDGE,"E15.left");var subQ18=sQuery(id+"F0.wireOp",EDGE,"E15.top");var subQ19=sQuery(id+"F0.wireOp",EDGE,"E14.trimOffspring");var subQ20=sQuery(id+"F0.wireOp",EDGE,"E13.right");var subQ21=sQuery(id+"F0.wireOp",EDGE,"E13.left");var subQ22=sQuery(id+"F0.wireOp",EDGE,"E13.top");var subQ23=sQuery(id+"F0.wireOp",EDGE,"E12.right");var subQ24=sQuery(id+"F0.wireOp",EDGE,"E12.top");var subQ25=sQuery(id+"F0.wireOp",EDGE,"E10.right");var subQ26=sQuery(id+"F0.wireOp",EDGE,"E10.left");var subQ27=sQuery(id+"F0.wireOp",EDGE,"E10.top");var subQ28=sQuery(id+"F0.wireOp",EDGE,"E9");var subQ29=sQuery(id+"F0.wireOp",EDGE,"E8");var subQ30=sQuery(id+"F0.wireOp",EDGE,"E7");var subQ31=sQuery(id+"F0.wireOp",EDGE,"E6");var subQ32=sQuery(id+"F0.wireOp",EDGE,"E5");var subQ33=sQuery(id+"F0.wireOp",EDGE,"E4");var subQ34=sQuery(id+"F0.wireOp",EDGE,"E3.trimOffspring");var subQ35=sQuery(id+"F0.wireOp",EDGE,"E1.right");var subQ36=sQuery(id+"F0.wireOp",EDGE,"E1.left");var subQ37=sQuery(id+"F0.wireOp",EDGE,"E1.top");var subQ38=sQuery(id+"F0.wireOp",EDGE,"E1.bottom");var subQ39=sQuery(id+"F0.wireOp",EDGE,"E0.right");var subQ40=sQuery(id+"F0.wireOp",EDGE,"E0.left");var subQ41=sQuery(id+"F0.wireOp",EDGE,"E0.bottom");Q1=makeQuery(id+"F19.boolean.opBoolean","MERGE",FACE,{"derivedFrom":[makeQuery(id+"F15.boolean.opBoolean","MERGE",FACE,{"derivedFrom":[makeQuery(id+"F9.boolean.opBoolean","MERGE",FACE,{"derivedFrom":[makeQuery(id+"F7.boolean.opBoolean","MERGE",FACE,{"derivedFrom":[makeQuery(id+"F5.boolean.opBoolean","MERGE",FACE,{"derivedFrom":[makeQuery(id+"F1.opExtrude","CAP_FACE",FACE,{"disambiguationData":[OSD([subQ41,subQ40,subQ39,subQ38,subQ37,subQ36,subQ35,subQ34,subQ33,subQ32,subQ31,subQ30,subQ29,subQ28,subQ27,subQ26,subQ25,subQ24,subQ23,subQ22,subQ21,subQ20,subQ19,subQ18,subQ17,subQ16,subQ15,subQ14,subQ13,subQ12,subQ11,subQ10,subQ9,subQ8,subQ7,subQ6,subQ5,subQ4,subQ3,subQ2,subQ1,subQ0])],"isStart":false}),makeQuery(id+"F5.opExtrude","CAP_FACE",FACE,{"disambiguationData":[OSD([subQ41,subQ40,subQ39,subQ38,subQ37,subQ36,subQ35,subQ34,subQ33,subQ32,subQ31,subQ30,subQ29,subQ28,subQ27,subQ26,subQ25,subQ24,subQ23,subQ22,subQ21,subQ20,subQ19,subQ18,subQ17,subQ16,subQ15,subQ14,subQ13,subQ12,subQ11,subQ10,subQ9,subQ8,subQ7,subQ6,subQ5,subQ4,subQ3,subQ2,subQ1,subQ0])],"isStart":false})]}),makeQuery(id+"F7.opExtrude","CAP_FACE",FACE,{"disambiguationData":[OSD([subQ41,subQ40,subQ39,subQ38,subQ37,subQ36,subQ35,subQ34,subQ33,subQ32,subQ31,subQ30,subQ29,subQ28,subQ27,subQ26,subQ25,subQ24,subQ23,subQ22,subQ21,subQ20,subQ19,subQ18,subQ17,subQ16,subQ15,subQ14,subQ13,subQ12,subQ11,subQ10,subQ9,subQ8,subQ7,subQ6,subQ5,subQ4,subQ3,subQ2,subQ1,subQ0])],"isStart":false})]}),makeQuery(id+"F9.opExtrude","CAP_FACE",FACE,{"disambiguationData":[OSD([subQ41,subQ40,subQ39,subQ38,subQ37,subQ36,subQ35,subQ34,subQ33,subQ32,subQ31,subQ30,subQ29,subQ28,subQ27,subQ26,subQ25,subQ24,subQ23,subQ22,subQ21,subQ20,subQ19,subQ18,subQ17,subQ16,subQ15,subQ14,subQ13,subQ12,subQ11,subQ10,subQ9,subQ8,subQ7,subQ6,subQ5,subQ4,subQ3,subQ2,subQ1,subQ0])],"isStart":false})]}),makeQuery(id+"F15.opExtrude","CAP_FACE",FACE,{"disambiguationData":[OSD([subQ41,subQ40,subQ39,subQ38,subQ37,subQ36,subQ35,subQ34,subQ33,subQ32,subQ31,subQ30,subQ29,subQ28,subQ27,subQ26,subQ25,subQ24,subQ23,subQ22,subQ21,subQ20,subQ19,subQ18,subQ17,subQ16,subQ15,subQ14,subQ13,subQ12,subQ11,subQ10,subQ9,subQ8,subQ7,subQ6,subQ5,subQ4,subQ3,subQ2,subQ1,subQ0])],"isStart":false})]}),makeQuery(id+"F19.opExtrude","CAP_FACE",FACE,{"disambiguationData":[OSD([subQ41,subQ40,subQ39,subQ38,subQ37,subQ36,subQ35,subQ34,subQ33,subQ32,subQ31,subQ30,subQ29,subQ28,subQ27,subQ26,subQ25,subQ24,subQ23,subQ22,subQ21,subQ20,subQ19,subQ18,subQ17,subQ16,subQ15,subQ14,subQ13,subQ12,subQ11,subQ10,subQ9,subQ8,subQ7,subQ6,subQ5,subQ4,subQ3,subQ2,subQ1,subQ0])],"isStart":false})]});}
            extrude(context, id + "F37", {"entities" : qUnion([Q0]), "operationType" : NewBodyOperationType.ADD, "endBound" : BoundingType.UP_TO_SURFACE, "depth" : 25 * mm, "endBoundEntityFace" : qUnion([Q1]), "offsetDistance" : 25 * mm});
        }
        {
            var Q0;
            Q0=makeQuery(id+"F19.opExtrude","SWEPT_FACE",FACE,{"disambiguationData":[OSD([sQuery(id+"F18.wireOp",EDGE,"E39")])]});
            var sketch = newSketch(context, id + "F38", { "sketchPlane" : qUnion([Q0])});
            skLineSegment(sketch, "E58.bottom", {"start": v(-5313, 2251) * mm, "end": v(-4727, 2251) * mm});
            skLineSegment(sketch, "E58.top", {"start": v(-5313, 2065) * mm, "end": v(-4727, 2065) * mm});
            skLineSegment(sketch, "E58.left", {"start": v(-5313, 2251) * mm, "end": v(-5313, 2065) * mm});
            skLineSegment(sketch, "E58.right", {"start": v(-4727, 2251) * mm, "end": v(-4727, 2065) * mm});
            skSolve(sketch);
        }
        {
            var Q0;
            Q0=makeQuery(id+"F38.imprint","IMPRINT",FACE,{"disambiguationData":[TD([[makeQuery(id+"F38.imprint","IMPRINT",EDGE,{"derivedFrom":sQuery(id+"F38.wireOp",EDGE,"E58.bottom")}),-1.0]])]});
            extrude(context, id + "F39", {"entities" : qUnion([Q0]), "operationType" : NewBodyOperationType.REMOVE, "endBound" : BoundingType.UP_TO_NEXT, "oppositeDirection" : true, "depth" : 25 * mm, "offsetDistance" : 25 * mm});
        }
    });
